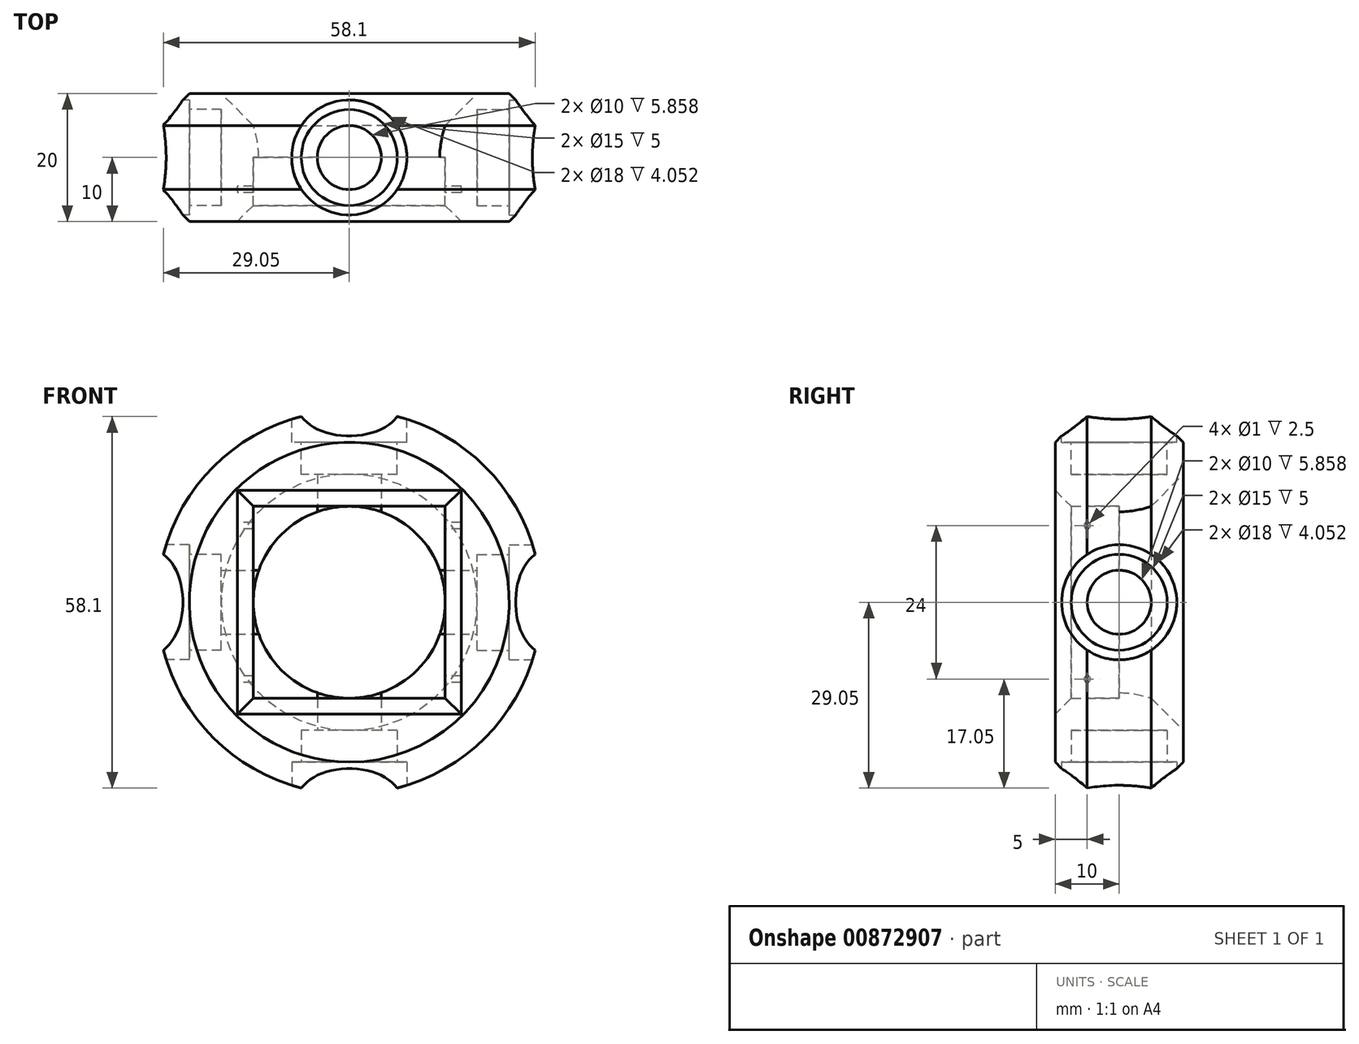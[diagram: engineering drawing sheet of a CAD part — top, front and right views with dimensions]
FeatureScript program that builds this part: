
annotation { "Feature Type Name" : "Feature", "Feature Type Description" : "" }
export const myFeature = defineFeature(function(context is Context, id is Id, definition is map)
    precondition{}
    {
        {
            var Q0;
            Q0=qCreatedBy(makeId("Front.planeOp"),FACE);
            var sketch = newSketch(context, id + "F0", { "sketchPlane" : qUnion([Q0])});
            skCircle(sketch, "E0", {"center": v(0, 0) * mm, "radius": 30 * mm});
            skCircle(sketch, "E1", {"center": v(0, 0) * mm, "radius": 15 * mm});
            skSolve(sketch);
        }
        {
            var Q0;
            Q0 = qSketchRegion(id + "F0", true);
            extrude(context, id + "F1", {"entities" : qUnion([Q0]), "endBound" : BoundingType.SYMMETRIC, "depth" : 20 * mm, "offsetDistance" : 25 * mm});
        }
        {
            var Q0;
            Q0=qCreatedBy(makeId("Top.planeOp"),FACE);
            cPlane(context, id + "F2", {"entities" : qUnion([Q0]), "cplaneType" : CPlaneType.OFFSET, "offset" : 30 * mm, "width" : 150 * mm, "height" : 150 * mm});
        }
        {
            var Q0;
            Q0=qCreatedBy(makeId("Top.planeOp"),FACE);
            cPlane(context, id + "F3", {"entities" : qUnion([Q0]), "cplaneType" : CPlaneType.OFFSET, "offset" : 30 * mm, "oppositeDirection" : true, "width" : 150 * mm, "height" : 150 * mm});
        }
        {
            var Q0;
            Q0=qCreatedBy(id+"F3.planeOp",FACE);
            var sketch = newSketch(context, id + "F4", { "sketchPlane" : qUnion([Q0])});
            skCircle(sketch, "E2", {"center": v(0, 0) * mm, "radius": 5 * mm});
            skSolve(sketch);
        }
        {
            var Q0;
            Q0 = qSketchRegion(id + "F4", true);
            extrude(context, id + "F5", {"entities" : qUnion([Q0]), "operationType" : NewBodyOperationType.REMOVE, "depth" : 77.4 * mm, "offsetDistance" : 25 * mm});
        }
        {
            var Q0;
            Q0=qCreatedBy(id+"F2.planeOp",FACE);
            var sketch = newSketch(context, id + "F6", { "sketchPlane" : qUnion([Q0])});
            skCircle(sketch, "E3", {"center": v(0, 0) * mm, "radius": 7.5 * mm});
            skSolve(sketch);
        }
        {
            var Q0;
            Q0 = qSketchRegion(id + "F6", true);
            extrude(context, id + "F7", {"entities" : qUnion([Q0]), "operationType" : NewBodyOperationType.REMOVE, "oppositeDirection" : true, "depth" : 10 * mm, "offsetDistance" : 25 * mm});
        }
        {
            var Q0;
            Q0=qCreatedBy(id+"F2.planeOp",FACE);
            var sketch = newSketch(context, id + "F8", { "sketchPlane" : qUnion([Q0])});
            skCircle(sketch, "E4", {"center": v(0, 0) * mm, "radius": 9 * mm});
            skSolve(sketch);
        }
        {
            var Q0;
            Q0 = qSketchRegion(id + "F8", true);
            extrude(context, id + "F9", {"entities" : qUnion([Q0]), "operationType" : NewBodyOperationType.REMOVE, "oppositeDirection" : true, "depth" : 5 * mm, "offsetDistance" : 25 * mm});
        }
        {
            var Q0;
            Q0=qCreatedBy(id+"F3.planeOp",FACE);
            var sketch = newSketch(context, id + "F10", { "sketchPlane" : qUnion([Q0])});
            skCircle(sketch, "E5", {"center": v(0, 0) * mm, "radius": 7.5 * mm});
            skSolve(sketch);
        }
        {
            var Q0;
            Q0 = qSketchRegion(id + "F10", true);
            extrude(context, id + "F11", {"entities" : qUnion([Q0]), "operationType" : NewBodyOperationType.REMOVE, "depth" : 10 * mm, "offsetDistance" : 25 * mm});
        }
        {
            var Q0;
            Q0=qCreatedBy(id+"F3.planeOp",FACE);
            var sketch = newSketch(context, id + "F12", { "sketchPlane" : qUnion([Q0])});
            skCircle(sketch, "E6", {"center": v(0, 0) * mm, "radius": 9 * mm});
            skSolve(sketch);
        }
        {
            var Q0;
            Q0 = qSketchRegion(id + "F12", true);
            extrude(context, id + "F13", {"entities" : qUnion([Q0]), "operationType" : NewBodyOperationType.REMOVE, "depth" : 5 * mm, "offsetDistance" : 25 * mm});
        }
        {
            var Q0;
            Q0=qCreatedBy(makeId("Right.planeOp"),FACE);
            cPlane(context, id + "F14", {"entities" : qUnion([Q0]), "cplaneType" : CPlaneType.OFFSET, "offset" : 30 * mm, "width" : 150 * mm, "height" : 150 * mm});
        }
        {
            var Q0;
            Q0=qCreatedBy(makeId("Right.planeOp"),FACE);
            cPlane(context, id + "F15", {"entities" : qUnion([Q0]), "cplaneType" : CPlaneType.OFFSET, "offset" : 30 * mm, "oppositeDirection" : true, "width" : 150 * mm, "height" : 150 * mm});
        }
        {
            var Q0;
            Q0=qCreatedBy(id+"F14.planeOp",FACE);
            var sketch = newSketch(context, id + "F16", { "sketchPlane" : qUnion([Q0])});
            skCircle(sketch, "E7", {"center": v(0, 0) * mm, "radius": 7.5 * mm});
            skSolve(sketch);
        }
        {
            var Q0;
            Q0 = qSketchRegion(id + "F16", true);
            extrude(context, id + "F17", {"entities" : qUnion([Q0]), "operationType" : NewBodyOperationType.REMOVE, "oppositeDirection" : true, "depth" : 10 * mm, "offsetDistance" : 25 * mm});
        }
        {
            var Q0;
            Q0=qCreatedBy(id+"F14.planeOp",FACE);
            var sketch = newSketch(context, id + "F18", { "sketchPlane" : qUnion([Q0])});
            skCircle(sketch, "E8", {"center": v(0, 0) * mm, "radius": 5 * mm});
            skSolve(sketch);
        }
        {
            var Q0;
            Q0 = qSketchRegion(id + "F18", true);
            extrude(context, id + "F19", {"entities" : qUnion([Q0]), "operationType" : NewBodyOperationType.REMOVE, "oppositeDirection" : true, "depth" : 88.4 * mm, "offsetDistance" : 25 * mm});
        }
        {
            var Q0;
            Q0=qCreatedBy(id+"F14.planeOp",FACE);
            var sketch = newSketch(context, id + "F20", { "sketchPlane" : qUnion([Q0])});
            skCircle(sketch, "E9", {"center": v(0, 0) * mm, "radius": 9 * mm});
            skSolve(sketch);
        }
        {
            var Q0;
            Q0 = qSketchRegion(id + "F20", true);
            extrude(context, id + "F21", {"entities" : qUnion([Q0]), "operationType" : NewBodyOperationType.REMOVE, "oppositeDirection" : true, "depth" : 5 * mm, "offsetDistance" : 25 * mm});
        }
        {
            var Q0;
            Q0=qCreatedBy(id+"F15.planeOp",FACE);
            var sketch = newSketch(context, id + "F22", { "sketchPlane" : qUnion([Q0])});
            skCircle(sketch, "E10", {"center": v(0, 0) * mm, "radius": 7.5 * mm});
            skSolve(sketch);
        }
        {
            var Q0;
            Q0 = qSketchRegion(id + "F22", true);
            extrude(context, id + "F23", {"entities" : qUnion([Q0]), "operationType" : NewBodyOperationType.REMOVE, "depth" : 10 * mm, "offsetDistance" : 25 * mm});
        }
        {
            var Q0;
            Q0=qCreatedBy(id+"F15.planeOp",FACE);
            var sketch = newSketch(context, id + "F24", { "sketchPlane" : qUnion([Q0])});
            skCircle(sketch, "E11", {"center": v(0, 0) * mm, "radius": 9 * mm});
            skSolve(sketch);
        }
        {
            var Q0;
            Q0 = qSketchRegion(id + "F24", true);
            extrude(context, id + "F25", {"entities" : qUnion([Q0]), "operationType" : NewBodyOperationType.REMOVE, "depth" : 5 * mm, "offsetDistance" : 25 * mm});
        }
        {
            var Q0;
            Q0=qCreatedBy(makeId("Front.planeOp"),FACE);
            var sketch = newSketch(context, id + "F26", { "sketchPlane" : qUnion([Q0])});
            skLineSegment(sketch, "E12.bottom", {"start": v(15, -15) * mm, "end": v(-15, -15) * mm});
            skLineSegment(sketch, "E12.top", {"start": v(15, 15) * mm, "end": v(-15, 15) * mm});
            skLineSegment(sketch, "E12.left", {"start": v(15, -15) * mm, "end": v(15, 15) * mm});
            skLineSegment(sketch, "E12.right", {"start": v(-15, -15) * mm, "end": v(-15, 15) * mm});
            skPoint(sketch, "E12.middle", {"position": v(0, 0) * mm});
            skSolve(sketch);
        }
        {
            var Q0;
            Q0 = qSketchRegion(id + "F26", true);
            extrude(context, id + "F27", {"entities" : qUnion([Q0]), "operationType" : NewBodyOperationType.REMOVE, "depth" : 21.4 * mm, "offsetDistance" : 25 * mm});
        }
        {
            var Q0;
            Q0=qCreatedBy(makeId("Right.planeOp"),FACE);
            var sketch = newSketch(context, id + "F28", { "sketchPlane" : qUnion([Q0])});
            skLineSegment(sketch, "E13", {"start": v(0, 0) * mm, "end": v(-5, 0) * mm, "construction": true});
            skLineSegment(sketch, "E14", {"start": v(-5, 0) * mm, "end": v(-5, 12) * mm, "construction": true});
            skCircle(sketch, "E15", {"center": v(-5, 12) * mm, "radius": 0.5 * mm});
            skLineSegment(sketch, "E16", {"start": v(-5, 0) * mm, "end": v(-5, -12) * mm, "construction": true});
            skCircle(sketch, "E17", {"center": v(-5, -12) * mm, "radius": 0.5 * mm});
            skSolve(sketch);
        }
        {
            var Q0;
            Q0 = qSketchRegion(id + "F28", true);
            extrude(context, id + "F29", {"entities" : qUnion([Q0]), "operationType" : NewBodyOperationType.REMOVE, "endBound" : BoundingType.SYMMETRIC, "depth" : 35 * mm, "offsetDistance" : 25 * mm});
        }
        {
            var Q0;
            Q0=qCreatedBy(makeId("Right.planeOp"),FACE);
            var sketch = newSketch(context, id + "F30", { "sketchPlane" : qUnion([Q0])});
            skLineSegment(sketch, "E18", {"start": v(0, 0) * mm, "end": v(-5, 0) * mm, "construction": true});
            skLineSegment(sketch, "E19", {"start": v(-5, 0) * mm, "end": v(-5, -12) * mm, "construction": true});
            skCircle(sketch, "E20", {"center": v(-5, -12) * mm, "radius": 0.5 * mm});
            skSolve(sketch);
        }
        {
            var Q0;
            Q0=makeQuery(id+"F30.imprint","IMPRINT",FACE,{"disambiguationData":[TD([[makeQuery(id+"F30.imprint","IMPRINT",EDGE,{"derivedFrom":sQuery(id+"F30.wireOp",EDGE,"E20")}),1.0]])]});
            extrude(context, id + "F31", {"entities" : qUnion([Q0]), "operationType" : NewBodyOperationType.REMOVE, "endBound" : BoundingType.SYMMETRIC, "oppositeDirection" : true, "depth" : 35 * mm, "offsetDistance" : 25 * mm});
        }
        {
            var Q0;
            Q0=makeQuery(id+"F1.opExtrude","CAP_EDGE",EDGE,{"disambiguationData":[OSD([sQuery(id+"F0.wireOp",EDGE,"E0")])],"isStart":true});
            chamfer(context, id + "F32", {"entities" : qUnion([Q0]), "width" : 5 * mm, "tangentPropagation" : true});
        }
        {
            var Q0;
            Q0=makeQuery(id+"F1.opExtrude","CAP_EDGE",EDGE,{"disambiguationData":[OSD([sQuery(id+"F0.wireOp",EDGE,"E0")])],"isStart":false});
            chamfer(context, id + "F33", {"entities" : qUnion([Q0]), "width" : 5 * mm, "tangentPropagation" : true});
        }
        {
            var Q0;
            Q0=makeQuery(id+"F1.opExtrude","CAP_EDGE",EDGE,{"disambiguationData":[OSD([sQuery(id+"F0.wireOp",EDGE,"E1")])],"isStart":true});
            chamfer(context, id + "F34", {"entities" : qUnion([Q0]), "width" : 5 * mm, "tangentPropagation" : true});
        }
        {
            var Q0;
            Q0=makeQuery(id+"F27.boolean.opBoolean","INTERSECT",EDGE,{"derivedFrom":[makeQuery(id+"F1.opExtrude","CAP_FACE",FACE,{"disambiguationData":[OSD([sQuery(id+"F0.wireOp",EDGE,"E0"),sQuery(id+"F0.wireOp",EDGE,"E1")])],"isStart":false}),makeQuery(id+"F27.opExtrude","SWEPT_FACE",FACE,{"disambiguationData":[OSD([sQuery(id+"F26.wireOp",EDGE,"E12.bottom")])]})]});
            chamfer(context, id + "F35", {"entities" : qUnion([Q0]), "width" : 2.5 * mm, "tangentPropagation" : true});
        }
        {
            var Q0;
            Q0=makeQuery(id+"F27.boolean.opBoolean","INTERSECT",EDGE,{"derivedFrom":[makeQuery(id+"F1.opExtrude","CAP_FACE",FACE,{"disambiguationData":[OSD([sQuery(id+"F0.wireOp",EDGE,"E0"),sQuery(id+"F0.wireOp",EDGE,"E1")])],"isStart":false}),makeQuery(id+"F27.opExtrude","SWEPT_FACE",FACE,{"disambiguationData":[OSD([sQuery(id+"F26.wireOp",EDGE,"E12.left")])]})]});
            chamfer(context, id + "F36", {"entities" : qUnion([Q0]), "width" : 2.5 * mm, "tangentPropagation" : true});
        }
        {
            var Q0;
            Q0=makeQuery(id+"F27.boolean.opBoolean","INTERSECT",EDGE,{"derivedFrom":[makeQuery(id+"F1.opExtrude","CAP_FACE",FACE,{"disambiguationData":[OSD([sQuery(id+"F0.wireOp",EDGE,"E0"),sQuery(id+"F0.wireOp",EDGE,"E1")])],"isStart":false}),makeQuery(id+"F27.opExtrude","SWEPT_FACE",FACE,{"disambiguationData":[OSD([sQuery(id+"F26.wireOp",EDGE,"E12.top")])]})]});
            var Q1;
            Q1=makeQuery(id+"F27.boolean.opBoolean","INTERSECT",EDGE,{"derivedFrom":[makeQuery(id+"F1.opExtrude","CAP_FACE",FACE,{"disambiguationData":[OSD([sQuery(id+"F0.wireOp",EDGE,"E0"),sQuery(id+"F0.wireOp",EDGE,"E1")])],"isStart":false}),makeQuery(id+"F27.opExtrude","SWEPT_FACE",FACE,{"disambiguationData":[OSD([sQuery(id+"F26.wireOp",EDGE,"E12.right")])]})]});
            chamfer(context, id + "F37", {"entities" : qUnion([Q0, Q1]), "width" : 2.5 * mm, "tangentPropagation" : true});
        }
    });
